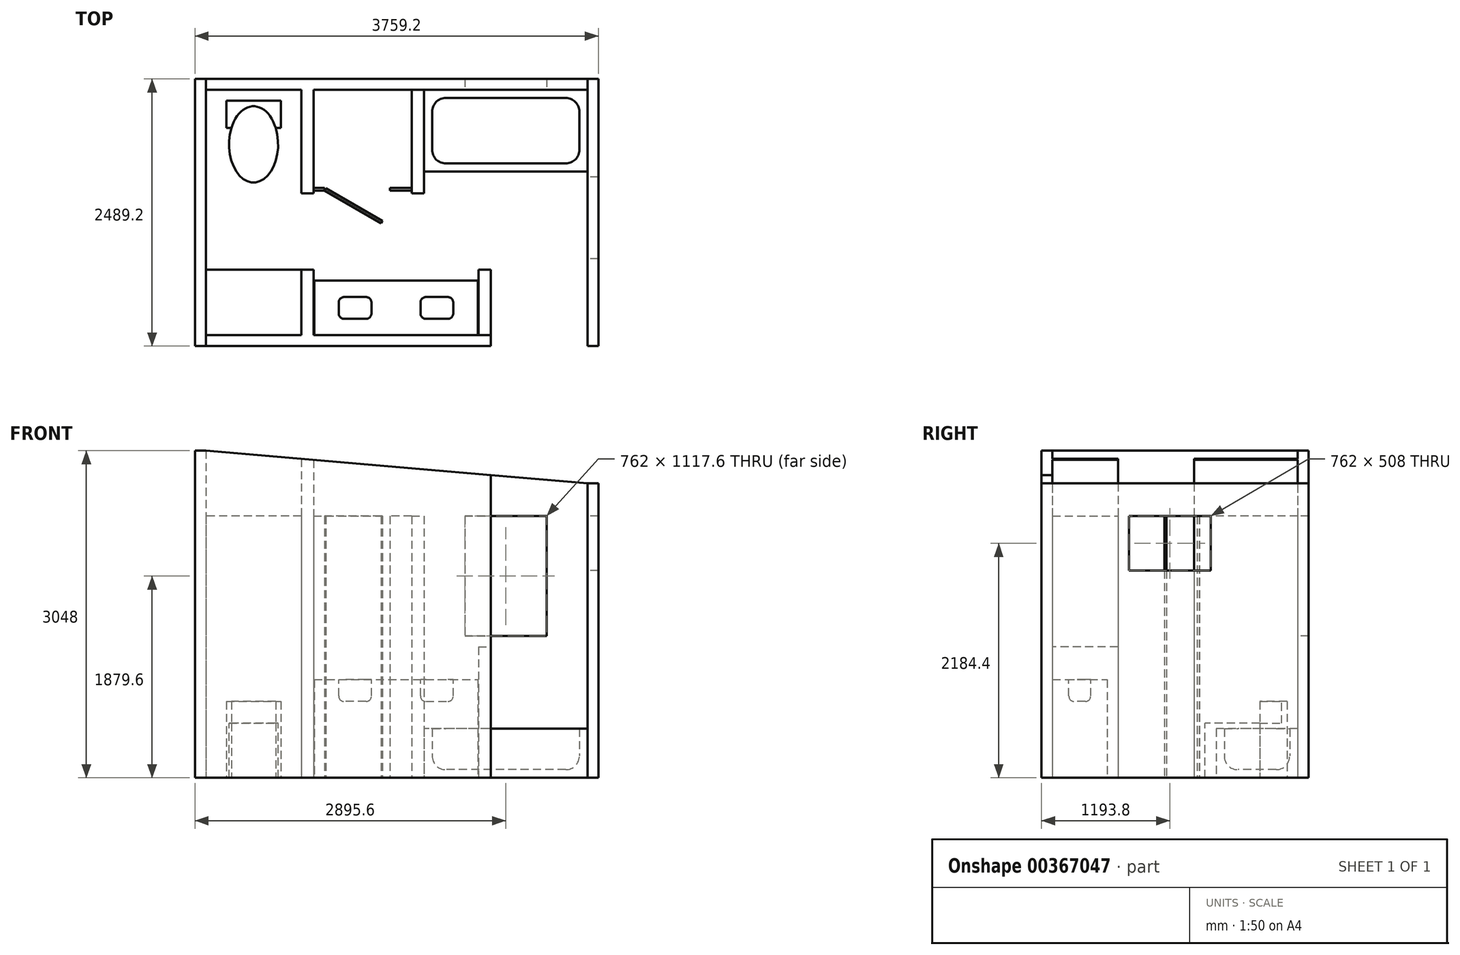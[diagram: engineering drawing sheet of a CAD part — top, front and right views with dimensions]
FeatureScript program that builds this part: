
annotation { "Feature Type Name" : "Feature", "Feature Type Description" : "" }
export const myFeature = defineFeature(function(context is Context, id is Id, definition is map)
    precondition{}
    {
        {
            var Q0;
            Q0=qCreatedBy(makeId("Top.planeOp"),FACE);
            var sketch = newSketch(context, id + "F0", { "sketchPlane" : qUnion([Q0])});
            skLineSegment(sketch, "E0.bottom", {"start": v(-3556, 2286) * mm, "end": v(0, 2286) * mm});
            skLineSegment(sketch, "E0.top", {"start": v(-3556, 0) * mm, "end": v(-901.7, 0) * mm});
            skLineSegment(sketch, "E0.left", {"start": v(-3556, 2286) * mm, "end": v(-3556, 0) * mm});
            skLineSegment(sketch, "E0.right", {"start": v(0, 2286) * mm, "end": v(0, -101.6) * mm});
            skLineSegment(sketch, "E1.0", {"start": v(-3657.6, 2387.6) * mm, "end": v(101.6, 2387.6) * mm});
            skLineSegment(sketch, "E1.1", {"start": v(-3657.6, 2387.6) * mm, "end": v(-3657.6, -101.6) * mm});
            skLineSegment(sketch, "E1.2", {"start": v(-3657.6, -101.6) * mm, "end": v(-901.7, -101.6) * mm});
            skLineSegment(sketch, "E1.3", {"start": v(101.6, 2387.6) * mm, "end": v(101.6, -101.6) * mm});
            skLineSegment(sketch, "E2", {"start": v(-901.7, 0) * mm, "end": v(-901.7, -101.6) * mm});
            skLineSegment(sketch, "E3", {"start": v(-901.7, 0) * mm, "end": v(0, 0) * mm, "construction": true});
            skLineSegment(sketch, "E4", {"start": v(-901.7, -101.6) * mm, "end": v(101.6, -101.6) * mm, "construction": true});
            skLineSegment(sketch, "E5", {"start": v(0, -101.6) * mm, "end": v(101.6, -101.6) * mm});
            skSolve(sketch);
        }
        {
            var Q0;
            Q0=qCreatedBy(makeId("Top.planeOp"),FACE);
            var sketch = newSketch(context, id + "F1", { "sketchPlane" : qUnion([Q0])});
            skLineSegment(sketch, "E6.0", {"start": v(-2667, 2286) * mm, "end": v(-2552.7, 2286) * mm});
            skLineSegment(sketch, "E7", {"start": v(-2667, 2286) * mm, "end": v(-2667, 1320.8) * mm});
            skLineSegment(sketch, "E8", {"start": v(-2667, 1320.8) * mm, "end": v(-2552.7, 1320.8) * mm});
            skLineSegment(sketch, "E9", {"start": v(-2552.7, 1320.8) * mm, "end": v(-2552.7, 2286) * mm});
            skPoint(sketch, "E10.orphan", {"position": v(0, 2286) * mm});
            skPoint(sketch, "E11.orphan", {"position": v(-3556, 2286) * mm});
            skLineSegment(sketch, "E12.bottom", {"start": v(-2667, 0) * mm, "end": v(-2552.7, 0) * mm});
            skLineSegment(sketch, "E12.top", {"start": v(-2667, 609.6) * mm, "end": v(-2552.7, 609.6) * mm});
            skLineSegment(sketch, "E12.left", {"start": v(-2667, 0) * mm, "end": v(-2667, 609.6) * mm});
            skLineSegment(sketch, "E12.right", {"start": v(-2552.7, 0) * mm, "end": v(-2552.7, 609.6) * mm});
            skLineSegment(sketch, "E13.bottom", {"start": v(-1638.3, 2286) * mm, "end": v(-1524, 2286) * mm});
            skLineSegment(sketch, "E13.top", {"start": v(-1638.3, 1320.8) * mm, "end": v(-1524, 1320.8) * mm});
            skLineSegment(sketch, "E13.left", {"start": v(-1638.3, 2286) * mm, "end": v(-1638.3, 1320.8) * mm});
            skLineSegment(sketch, "E13.right", {"start": v(-1524, 2286) * mm, "end": v(-1524, 1320.8) * mm});
            skLineSegment(sketch, "E14.bottom", {"start": v(-1016, 609.6) * mm, "end": v(-901.7, 609.6) * mm});
            skLineSegment(sketch, "E14.top", {"start": v(-1016, 0) * mm, "end": v(-901.7, 0) * mm});
            skLineSegment(sketch, "E14.left", {"start": v(-1016, 609.6) * mm, "end": v(-1016, 0) * mm});
            skLineSegment(sketch, "E14.right", {"start": v(-901.7, 609.6) * mm, "end": v(-901.7, 0) * mm});
            skSolve(sketch);
        }
        {
            var Q0;
            Q0 = qSketchRegion(id + "F0", true);
            extrude(context, id + "F2", {"entities" : qUnion([Q0]), "depth" : 3048 * mm});
        }
        {
            var Q0;
            Q0=makeQuery(id+"F1.imprint","IMPRINT",FACE,{"disambiguationData":[TD([[makeQuery(id+"F1.imprint","IMPRINT",EDGE,{"derivedFrom":sQuery(id+"F1.wireOp",EDGE,"E6.0")}),-1.0]])]});
            var Q1;
            Q1=makeQuery(id+"F1.imprint","IMPRINT",FACE,{"disambiguationData":[TD([[makeQuery(id+"F1.imprint","IMPRINT",EDGE,{"derivedFrom":sQuery(id+"F1.wireOp",EDGE,"E12.bottom")}),1.0]])]});
            var Q2;
            Q2=makeQuery(id+"F2.opExtrude","CAP_FACE",FACE,{"disambiguationData":[OSD([sQuery(id+"F0.wireOp",EDGE,"E0.bottom"),sQuery(id+"F0.wireOp",EDGE,"E0.top"),sQuery(id+"F0.wireOp",EDGE,"E0.left"),sQuery(id+"F0.wireOp",EDGE,"E0.right"),sQuery(id+"F0.wireOp",EDGE,"E1.0"),sQuery(id+"F0.wireOp",EDGE,"E1.1"),sQuery(id+"F0.wireOp",EDGE,"E1.2"),sQuery(id+"F0.wireOp",EDGE,"E1.3")])],"isStart":false});
            extrude(context, id + "F3", {"entities" : qUnion([Q0, Q1]), "operationType" : NewBodyOperationType.ADD, "endBound" : BoundingType.UP_TO_SURFACE, "endBoundEntityFace" : qUnion([Q2]), "depth" : 25.4 * mm});
        }
        {
            var Q0;
            Q0=makeQuery(id+"F1.imprint","IMPRINT",FACE,{"disambiguationData":[TD([[makeQuery(id+"F1.imprint","IMPRINT",EDGE,{"derivedFrom":sQuery(id+"F1.wireOp",EDGE,"E13.bottom")}),-1.0]])]});
            extrude(context, id + "F4", {"entities" : qUnion([Q0]), "operationType" : NewBodyOperationType.ADD, "depth" : 2438.4 * mm});
        }
        {
            var Q0;
            Q0=qCreatedBy(makeId("Front.planeOp"),FACE);
            var sketch = newSketch(context, id + "F5", { "sketchPlane" : qUnion([Q0])});
            skLineSegment(sketch, "E15", {"start": v(-3556, 3048) * mm, "end": v(0, 2743.2) * mm});
            skLineSegment(sketch, "E16.0", {"start": v(-3556, 3048) * mm, "end": v(101.6, 3048) * mm});
            skPoint(sketch, "E17.orphan", {"position": v(-3657.6, 3048) * mm});
            skLineSegment(sketch, "E18.0", {"start": v(0, 3048) * mm, "end": v(0, 2743.2) * mm});
            skPoint(sketch, "E19.orphan", {"position": v(-901.7, 3048) * mm});
            skPoint(sketch, "E20.orphan", {"position": v(0, 24.07) * mm});
            skPoint(sketch, "E21.orphan", {"position": v(-876.3, 0) * mm});
            skLineSegment(sketch, "E22.1", {"start": v(101.6, 3048) * mm, "end": v(101.6, 2743.2) * mm});
            skLineSegment(sketch, "E23", {"start": v(0, 2743.2) * mm, "end": v(101.6, 2743.2) * mm});
            skPoint(sketch, "E24.orphan", {"position": v(101.6, 0) * mm});
            skSolve(sketch);
        }
        {
            var Q0;
            Q0 = qSketchRegion(id + "F5", true);
            extrude(context, id + "F6", {"entities" : qUnion([Q0]), "operationType" : NewBodyOperationType.REMOVE, "endBound" : BoundingType.THROUGH_ALL, "oppositeDirection" : true, "depth" : 25.4 * mm, "hasSecondDirection" : true, "secondDirectionBound" : SecondDirectionBoundingType.THROUGH_ALL, "secondDirectionOppositeDirection" : false, "secondDirectionDepth" : 25.4 * mm});
        }
        {
            var Q0;
            Q0=qCreatedBy(makeId("Top.planeOp"),FACE);
            var sketch = newSketch(context, id + "F7", { "sketchPlane" : qUnion([Q0])});
            skLineSegment(sketch, "E25.bottom", {"start": v(0, 2286) * mm, "end": v(-1524, 2286) * mm});
            skLineSegment(sketch, "E25.top", {"start": v(0, 1524) * mm, "end": v(-1524, 1524) * mm});
            skLineSegment(sketch, "E25.left", {"start": v(0, 2286) * mm, "end": v(0, 1524) * mm});
            skLineSegment(sketch, "E25.right", {"start": v(-1524, 2286) * mm, "end": v(-1524, 1524) * mm});
            skSolve(sketch);
        }
        {
            var Q0;
            Q0=makeQuery(id+"F7.imprint","IMPRINT",FACE,{"disambiguationData":[TD([[makeQuery(id+"F7.imprint","IMPRINT",EDGE,{"derivedFrom":sQuery(id+"F7.wireOp",EDGE,"E25.bottom")}),1.0]])]});
            extrude(context, id + "F8", {"entities" : qUnion([Q0]), "depth" : 457.2 * mm});
        }
        {
            var Q0;
            Q0=makeQuery(id+"F8.opExtrude","CAP_FACE",FACE,{"disambiguationData":[OSD([sQuery(id+"F7.wireOp",EDGE,"E25.bottom"),sQuery(id+"F7.wireOp",EDGE,"E25.top"),sQuery(id+"F7.wireOp",EDGE,"E25.left"),sQuery(id+"F7.wireOp",EDGE,"E25.right")])],"isStart":false});
            shell(context, id + "F9", {"entities" : qUnion([Q0]), "thickness" : 76.2 * mm});
        }
        {
            var Q0;
            Q0=makeQuery(id+"F9.opShell","OFFSET_EDGE",EDGE,{"disambiguationData":[OSD([sQuery(id+"F7.wireOp",EDGE,"E25.top"),sQuery(id+"F7.wireOp",EDGE,"E25.right")])]});
            var Q1;
            Q1=makeQuery(id+"F9.opShell","OFFSET_EDGE",EDGE,{"disambiguationData":[OSD([sQuery(id+"F7.wireOp",EDGE,"E25.bottom"),sQuery(id+"F7.wireOp",EDGE,"E25.right")])]});
            var Q2;
            Q2=makeQuery(id+"F9.opShell","OFFSET_EDGE",EDGE,{"disambiguationData":[OSD([sQuery(id+"F7.wireOp",EDGE,"E25.top"),sQuery(id+"F7.wireOp",EDGE,"E25.left")])]});
            var Q3;
            Q3=makeQuery(id+"F9.opShell","OFFSET_EDGE",EDGE,{"disambiguationData":[OSD([sQuery(id+"F7.wireOp",EDGE,"E25.bottom"),sQuery(id+"F7.wireOp",EDGE,"E25.left")])]});
            var Q4;
            Q4=makeQuery(id+"F9.opShell","OFFSET_FACE",FACE,{"disambiguationData":[OSD([sQuery(id+"F7.wireOp",EDGE,"E25.bottom"),sQuery(id+"F7.wireOp",EDGE,"E25.top"),sQuery(id+"F7.wireOp",EDGE,"E25.left"),sQuery(id+"F7.wireOp",EDGE,"E25.right")])]});
            fillet(context, id + "F10", {"entities" : qUnion([Q0, Q1, Q2, Q3, Q4]), "radius" : 127 * mm, "tangentPropagation" : true, "allowEdgeOverflow" : false});
        }
        {
            var Q0;
            Q0=qCreatedBy(makeId("Top.planeOp"),FACE);
            var sketch = newSketch(context, id + "F11", { "sketchPlane" : qUnion([Q0])});
            skLineSegment(sketch, "E26.right", {"start": v(-1841.5, 1371.6) * mm, "end": v(-1841.5, 1346.2) * mm});
            skLineSegment(sketch, "E27", {"start": v(-1841.5, 1346.2) * mm, "end": v(-1638.3, 1346.2) * mm});
            skLineSegment(sketch, "E28", {"start": v(-1638.3, 1346.2) * mm, "end": v(-1638.3, 1371.6) * mm});
            skLineSegment(sketch, "E29", {"start": v(-1638.3, 1371.6) * mm, "end": v(-1841.5, 1371.6) * mm});
            skLineSegment(sketch, "E30", {"start": v(-1923.17, 1041.4) * mm, "end": v(-2451.1, 1346.2) * mm});
            skLineSegment(sketch, "E31", {"start": v(-2451.1, 1346.2) * mm, "end": v(-2438.4, 1368.2) * mm});
            skLineSegment(sketch, "E32", {"start": v(-2438.4, 1368.2) * mm, "end": v(-1910.47, 1063.4) * mm});
            skLineSegment(sketch, "E33", {"start": v(-1910.47, 1063.4) * mm, "end": v(-1923.17, 1041.4) * mm});
            skLineSegment(sketch, "E34", {"start": v(-1841.5, 1371.6) * mm, "end": v(-2552.7, 1371.6) * mm, "construction": true});
            skLineSegment(sketch, "E35.bottom", {"start": v(-2552.7, 1371.6) * mm, "end": v(-2451.1, 1371.6) * mm});
            skLineSegment(sketch, "E35.top", {"start": v(-2552.7, 1346.2) * mm, "end": v(-2451.1, 1346.2) * mm});
            skLineSegment(sketch, "E35.left", {"start": v(-2552.7, 1371.6) * mm, "end": v(-2552.7, 1346.2) * mm});
            skLineSegment(sketch, "E35.right", {"start": v(-2451.1, 1371.6) * mm, "end": v(-2451.1, 1346.2) * mm});
            skSolve(sketch);
        }
        {
            var Q0;
            Q0=makeQuery(id+"F11.imprint","IMPRINT",FACE,{"disambiguationData":[TD([[makeQuery(id+"F11.imprint","IMPRINT",EDGE,{"derivedFrom":sQuery(id+"F11.wireOp",EDGE,"E30")}),-1.0]])]});
            var Q1;
            Q1=makeQuery(id+"F4.opExtrude","CAP_FACE",FACE,{"disambiguationData":[OSD([sQuery(id+"F1.wireOp",EDGE,"E13.bottom"),sQuery(id+"F1.wireOp",EDGE,"E13.top"),sQuery(id+"F1.wireOp",EDGE,"E13.left"),sQuery(id+"F1.wireOp",EDGE,"E13.right")])],"isStart":false});
            extrude(context, id + "F12", {"entities" : qUnion([Q0]), "endBound" : BoundingType.UP_TO_SURFACE, "endBoundEntityFace" : qUnion([Q1]), "depth" : 25.4 * mm});
        }
        {
            var Q0;
            Q0=makeQuery(id+"F11.imprint","IMPRINT",FACE,{"disambiguationData":[TD([[makeQuery(id+"F11.imprint","IMPRINT",EDGE,{"derivedFrom":sQuery(id+"F11.wireOp",EDGE,"E27")}),1.0]])]});
            var Q1;
            Q1=makeQuery(id+"F11.imprint","IMPRINT",FACE,{"disambiguationData":[TD([[makeQuery(id+"F11.imprint","IMPRINT",EDGE,{"derivedFrom":sQuery(id+"F11.wireOp",EDGE,"E35.bottom")}),-1.0]])]});
            var Q2;
            Q2=makeQuery(id+"F4.opExtrude","CAP_FACE",FACE,{"disambiguationData":[OSD([sQuery(id+"F1.wireOp",EDGE,"E13.bottom"),sQuery(id+"F1.wireOp",EDGE,"E13.top"),sQuery(id+"F1.wireOp",EDGE,"E13.left"),sQuery(id+"F1.wireOp",EDGE,"E13.right")])],"isStart":false});
            extrude(context, id + "F13", {"entities" : qUnion([Q0, Q1]), "endBound" : BoundingType.UP_TO_SURFACE, "endBoundEntityFace" : qUnion([Q2]), "depth" : 25.4 * mm});
        }
        {
            var Q0;
            {var subQ0=sQuery(id+"F0.wireOp",EDGE,"E0.right");var subQ9=sQuery(id+"F0.wireOp",EDGE,"E0.bottom");Q0=makeQuery(id+"F3.boolean.opBoolean","SPLIT",FACE,{"disambiguationData":[TD([makeQuery(id+"F2.opExtrude","SWEPT_FACE",FACE,{"disambiguationData":[OSD([subQ0])]})])],"derivedFrom":makeQuery(id+"F2.opExtrude","SWEPT_FACE",FACE,{"disambiguationData":[OSD([subQ9])]})});}
            var sketch = newSketch(context, id + "F14", { "sketchPlane" : qUnion([Q0])});
            skLineSegment(sketch, "E36", {"start": v(-762, 1879.6) * mm, "end": v(-762, 457.2) * mm, "construction": true});
            skLineSegment(sketch, "E37.bottom", {"start": v(-1143, 2438.4) * mm, "end": v(-381, 2438.4) * mm});
            skLineSegment(sketch, "E37.top", {"start": v(-1143, 1320.8) * mm, "end": v(-381, 1320.8) * mm});
            skLineSegment(sketch, "E37.left", {"start": v(-1143, 2438.4) * mm, "end": v(-1143, 1320.8) * mm});
            skLineSegment(sketch, "E37.right", {"start": v(-381, 2438.4) * mm, "end": v(-381, 1320.8) * mm});
            skPoint(sketch, "E37.middle", {"position": v(-762, 1879.6) * mm});
            skSolve(sketch);
        }
        {
            var Q0;
            Q0 = qSketchRegion(id + "F14", true);
            extrude(context, id + "F15", {"entities" : qUnion([Q0]), "operationType" : NewBodyOperationType.REMOVE, "endBound" : BoundingType.THROUGH_ALL, "oppositeDirection" : true, "depth" : 25.4 * mm});
        }
        {
            var Q0;
            Q0=qCreatedBy(makeId("Top.planeOp"),FACE);
            var sketch = newSketch(context, id + "F16", { "sketchPlane" : qUnion([Q0])});
            skLineSegment(sketch, "E38.bottom", {"start": v(-2546.35, 0) * mm, "end": v(-1022.35, 0) * mm});
            skLineSegment(sketch, "E38.top", {"start": v(-2546.35, 508) * mm, "end": v(-1022.35, 508) * mm});
            skLineSegment(sketch, "E38.left", {"start": v(-2546.35, 0) * mm, "end": v(-2546.35, 508) * mm});
            skLineSegment(sketch, "E38.right", {"start": v(-1022.35, 0) * mm, "end": v(-1022.35, 508) * mm});
            skPoint(sketch, "E39.orphan", {"position": v(-901.7, 0) * mm});
            skPoint(sketch, "E40.1.start.orphan", {"position": v(-1016, 609.6) * mm});
            skPoint(sketch, "E40.0.end.orphan", {"position": v(-2552.7, 0) * mm});
            skPoint(sketch, "E40.0.start.orphan", {"position": v(-1016, 0) * mm});
            skLineSegment(sketch, "E41", {"start": v(-2552.7, 304.8) * mm, "end": v(-1016, 304.8) * mm, "construction": true});
            skLineSegment(sketch, "E42", {"start": v(-1784.35, 304.8) * mm, "end": v(-1784.35, 508) * mm, "construction": true});
            skSolve(sketch);
        }
        {
            var Q0;
            Q0 = qSketchRegion(id + "F16", true);
            extrude(context, id + "F17", {"entities" : qUnion([Q0]), "depth" : 914.4 * mm});
        }
        {
            var Q0;
            Q0=makeQuery(id+"F17.opExtrude","CAP_FACE",FACE,{"disambiguationData":[OSD([sQuery(id+"F16.wireOp",EDGE,"E38.bottom"),sQuery(id+"F16.wireOp",EDGE,"E38.top"),sQuery(id+"F16.wireOp",EDGE,"E38.left"),sQuery(id+"F16.wireOp",EDGE,"E38.right")])],"isStart":false});
            var sketch = newSketch(context, id + "F18", { "sketchPlane" : qUnion([Q0])});
            skLineSegment(sketch, "E43.0", {"start": v(-2546.35, 508) * mm, "end": v(-2165.35, 508) * mm, "construction": true});
            skLineSegment(sketch, "E44", {"start": v(-2165.35, 508) * mm, "end": v(-1784.35, 508) * mm, "construction": true});
            skLineSegment(sketch, "E45", {"start": v(-1784.35, 508) * mm, "end": v(-1403.35, 508) * mm, "construction": true});
            skLineSegment(sketch, "E46", {"start": v(-1403.35, 508) * mm, "end": v(-1022.35, 508) * mm, "construction": true});
            skLineSegment(sketch, "E47", {"start": v(-2165.35, 508) * mm, "end": v(-2165.35, 0) * mm, "construction": true});
            skLineSegment(sketch, "E48", {"start": v(-1403.35, 508) * mm, "end": v(-1403.35, 0) * mm, "construction": true});
            skLineSegment(sketch, "E49.bottom", {"start": v(-2012.95, 355.6) * mm, "end": v(-2317.75, 355.6) * mm});
            skLineSegment(sketch, "E49.top", {"start": v(-2012.95, 152.4) * mm, "end": v(-2317.75, 152.4) * mm});
            skLineSegment(sketch, "E49.left", {"start": v(-2012.95, 355.6) * mm, "end": v(-2012.95, 152.4) * mm});
            skLineSegment(sketch, "E49.right", {"start": v(-2317.75, 355.6) * mm, "end": v(-2317.75, 152.4) * mm});
            skPoint(sketch, "E49.middle", {"position": v(-2165.35, 254) * mm});
            skLineSegment(sketch, "E50.bottom", {"start": v(-1555.75, 355.6) * mm, "end": v(-1250.95, 355.6) * mm});
            skLineSegment(sketch, "E50.top", {"start": v(-1555.75, 152.4) * mm, "end": v(-1250.95, 152.4) * mm});
            skLineSegment(sketch, "E50.left", {"start": v(-1555.75, 355.6) * mm, "end": v(-1555.75, 152.4) * mm});
            skLineSegment(sketch, "E50.right", {"start": v(-1250.95, 355.6) * mm, "end": v(-1250.95, 152.4) * mm});
            skPoint(sketch, "E50.middle", {"position": v(-1403.35, 254) * mm});
            skSolve(sketch);
        }
        {
            var Q0;
            Q0 = qSketchRegion(id + "F18", true);
            extrude(context, id + "F19", {"entities" : qUnion([Q0]), "operationType" : NewBodyOperationType.REMOVE, "oppositeDirection" : true, "depth" : 203.2 * mm});
        }
        {
            var Q0;
            Q0=makeQuery(id+"F19.boolean.opBoolean","COPY",EDGE,{"derivedFrom":makeQuery(id+"F19.opExtrude","SWEPT_EDGE",EDGE,{"disambiguationData":[OSD([sQuery(id+"F18.wireOp",EDGE,"E49.bottom"),sQuery(id+"F18.wireOp",EDGE,"E49.right")])]})});
            var Q1;
            Q1=makeQuery(id+"F19.boolean.opBoolean","COPY",EDGE,{"derivedFrom":makeQuery(id+"F19.opExtrude","SWEPT_EDGE",EDGE,{"disambiguationData":[OSD([sQuery(id+"F18.wireOp",EDGE,"E49.bottom"),sQuery(id+"F18.wireOp",EDGE,"E49.left")])]})});
            var Q2;
            Q2=makeQuery(id+"F19.boolean.opBoolean","COPY",EDGE,{"derivedFrom":makeQuery(id+"F19.opExtrude","SWEPT_EDGE",EDGE,{"disambiguationData":[OSD([sQuery(id+"F18.wireOp",EDGE,"E49.top"),sQuery(id+"F18.wireOp",EDGE,"E49.right")])]})});
            var Q3;
            Q3=makeQuery(id+"F19.boolean.opBoolean","COPY",EDGE,{"derivedFrom":makeQuery(id+"F19.opExtrude","SWEPT_EDGE",EDGE,{"disambiguationData":[OSD([sQuery(id+"F18.wireOp",EDGE,"E49.top"),sQuery(id+"F18.wireOp",EDGE,"E49.left")])]})});
            var Q4;
            Q4=makeQuery(id+"F19.boolean.opBoolean","COPY",FACE,{"derivedFrom":makeQuery(id+"F19.opExtrude","CAP_FACE",FACE,{"disambiguationData":[OSD([sQuery(id+"F18.wireOp",EDGE,"E49.bottom"),sQuery(id+"F18.wireOp",EDGE,"E49.top"),sQuery(id+"F18.wireOp",EDGE,"E49.left"),sQuery(id+"F18.wireOp",EDGE,"E49.right")])],"isStart":false})});
            var Q5;
            Q5=makeQuery(id+"F19.boolean.opBoolean","COPY",EDGE,{"derivedFrom":makeQuery(id+"F19.opExtrude","SWEPT_EDGE",EDGE,{"disambiguationData":[OSD([sQuery(id+"F18.wireOp",EDGE,"E50.top"),sQuery(id+"F18.wireOp",EDGE,"E50.right")])]})});
            var Q6;
            Q6=makeQuery(id+"F19.boolean.opBoolean","COPY",EDGE,{"derivedFrom":makeQuery(id+"F19.opExtrude","SWEPT_EDGE",EDGE,{"disambiguationData":[OSD([sQuery(id+"F18.wireOp",EDGE,"E50.top"),sQuery(id+"F18.wireOp",EDGE,"E50.left")])]})});
            var Q7;
            Q7=makeQuery(id+"F19.boolean.opBoolean","COPY",EDGE,{"derivedFrom":makeQuery(id+"F19.opExtrude","SWEPT_EDGE",EDGE,{"disambiguationData":[OSD([sQuery(id+"F18.wireOp",EDGE,"E50.bottom"),sQuery(id+"F18.wireOp",EDGE,"E50.right")])]})});
            var Q8;
            Q8=makeQuery(id+"F19.boolean.opBoolean","COPY",EDGE,{"derivedFrom":makeQuery(id+"F19.opExtrude","SWEPT_EDGE",EDGE,{"disambiguationData":[OSD([sQuery(id+"F18.wireOp",EDGE,"E50.bottom"),sQuery(id+"F18.wireOp",EDGE,"E50.left")])]})});
            var Q9;
            Q9=makeQuery(id+"F19.boolean.opBoolean","COPY",FACE,{"derivedFrom":makeQuery(id+"F19.opExtrude","CAP_FACE",FACE,{"disambiguationData":[OSD([sQuery(id+"F18.wireOp",EDGE,"E50.bottom"),sQuery(id+"F18.wireOp",EDGE,"E50.top"),sQuery(id+"F18.wireOp",EDGE,"E50.left"),sQuery(id+"F18.wireOp",EDGE,"E50.right")])],"isStart":false})});
            fillet(context, id + "F20", {"entities" : qUnion([Q0, Q1, Q2, Q3, Q4, Q5, Q6, Q7, Q8, Q9]), "radius" : 50.8 * mm, "tangentPropagation" : true, "allowEdgeOverflow" : false});
        }
        {
            var Q0;
            Q0=qCreatedBy(makeId("Top.planeOp"),FACE);
            var sketch = newSketch(context, id + "F21", { "sketchPlane" : qUnion([Q0])});
            skEllipse(sketch, "E51", {"center": v(-3111.5, 1778) * mm, "majorRadius": 355.6 * mm, "minorRadius": 228.6 * mm, "majorAxis": v(0, 1)});
            skLineSegment(sketch, "E52", {"start": v(-3111.5, 1778) * mm, "end": v(-3111.5, 2286) * mm, "construction": true});
            skPoint(sketch, "E52.endSnap0", {"position": v(-3111.5, 2133.6) * mm});
            skLineSegment(sketch, "E53.bottom", {"start": v(-3365.5, 2184.4) * mm, "end": v(-2857.5, 2184.4) * mm});
            skLineSegment(sketch, "E53.top", {"start": v(-3365.5, 1930.4) * mm, "end": v(-2857.5, 1930.4) * mm});
            skLineSegment(sketch, "E53.left", {"start": v(-3365.5, 2184.4) * mm, "end": v(-3365.5, 1930.4) * mm});
            skLineSegment(sketch, "E53.right", {"start": v(-2857.5, 2184.4) * mm, "end": v(-2857.5, 1930.4) * mm});
            skPoint(sketch, "E53.middle", {"position": v(-3111.5, 2057.4) * mm});
            skLineSegment(sketch, "E54", {"start": v(-3111.5, 1778) * mm, "end": v(-3111.5, 1422.4) * mm, "construction": true});
            skSolve(sketch);
        }
        {
            var Q0;
            Q0=makeQuery(id+"F21.imprint","IMPRINT",FACE,{"disambiguationData":[TD([[makeQuery(id+"F21.imprint","IMPRINT",EDGE,{"derivedFrom":sQuery(id+"F21.wireOp",EDGE,"E51")}),1.0]])]});
            extrude(context, id + "F22", {"entities" : qUnion([Q0]), "depth" : 508 * mm});
        }
        {
            var Q0;
            Q0=makeQuery(id+"F21.imprint","IMPRINT",FACE,{"disambiguationData":[TD([[makeQuery(id+"F21.imprint","IMPRINT",EDGE,{"derivedFrom":sQuery(id+"F21.wireOp",EDGE,"E53.bottom")}),-1.0]])]});
            extrude(context, id + "F23", {"entities" : qUnion([Q0]), "operationType" : NewBodyOperationType.ADD, "depth" : 711.2 * mm});
        }
        {
            var Q0;
            Q0=qCreatedBy(makeId("Top.planeOp"),FACE);
            var sketch = newSketch(context, id + "F24", { "sketchPlane" : qUnion([Q0])});
            skLineSegment(sketch, "E55.bottom", {"start": v(-2667, 0) * mm, "end": v(-3556, 0) * mm});
            skLineSegment(sketch, "E55.top", {"start": v(-2667, 609.6) * mm, "end": v(-3556, 609.6) * mm});
            skLineSegment(sketch, "E55.left", {"start": v(-2667, 0) * mm, "end": v(-2667, 609.6) * mm});
            skLineSegment(sketch, "E55.right", {"start": v(-3556, 0) * mm, "end": v(-3556, 609.6) * mm});
            skSolve(sketch);
        }
        {
            var Q0;
            Q0 = qSketchRegion(id + "F24", true);
            extrude(context, id + "F25", {"entities" : qUnion([Q0]), "depth" : 2438.4 * mm});
        }
        {
            var Q0;
            Q0=makeQuery(id+"FOXC9kZpfs4iDAW_4.boolean.opBoolean","MERGE",FACE,{"derivedFrom":[makeQuery(id+"F2.opExtrude","SWEPT_FACE",FACE,{"disambiguationData":[OSD([sQuery(id+"F0.wireOp",EDGE,"E0.right")])]}),makeQuery(id+"FOXC9kZpfs4iDAW_4.opExtrude","SWEPT_FACE",FACE,{"disambiguationData":[OSD([sQuery(id+"F0lmWyXV5AHyWku_4.wireOp",EDGE,"oQEbStr6-n6Tl-aHSC-o00H-vOLfrQHnq2UT.left")])]})]});
            var sketch = newSketch(context, id + "F26", { "sketchPlane" : qUnion([Q0])});
            skPoint(sketch, "E56.orphan", {"position": v(-2286, 2743.2) * mm});
            skPoint(sketch, "E57.orphan", {"position": v(101.6, 2743.2) * mm});
            skLineSegment(sketch, "E58.bottom", {"start": v(-1473.2, 2438.4) * mm, "end": v(-711.2, 2438.4) * mm});
            skLineSegment(sketch, "E58.top", {"start": v(-1473.2, 1930.4) * mm, "end": v(-711.2, 1930.4) * mm});
            skLineSegment(sketch, "E58.left", {"start": v(-1473.2, 2438.4) * mm, "end": v(-1473.2, 1930.4) * mm});
            skLineSegment(sketch, "E58.right", {"start": v(-711.2, 2438.4) * mm, "end": v(-711.2, 1930.4) * mm});
            skLineSegment(sketch, "E59", {"start": v(-1092.2, 2438.4) * mm, "end": v(-1092.2, 2743.2) * mm, "construction": true});
            skSolve(sketch);
        }
        {
            var Q0;
            Q0 = qSketchRegion(id + "F26", true);
            extrude(context, id + "F27", {"entities" : qUnion([Q0]), "operationType" : NewBodyOperationType.REMOVE, "endBound" : BoundingType.THROUGH_ALL, "oppositeDirection" : true, "depth" : 25.4 * mm});
        }
        {
            var Q0;
            Q0=makeQuery(id+"F1.imprint","IMPRINT",FACE,{"disambiguationData":[TD([[makeQuery(id+"F1.imprint","IMPRINT",EDGE,{"derivedFrom":sQuery(id+"F1.wireOp",EDGE,"E14.bottom")}),-1.0]])]});
            extrude(context, id + "F28", {"entities" : qUnion([Q0]), "operationType" : NewBodyOperationType.ADD, "depth" : 1219.2 * mm});
        }
    });
